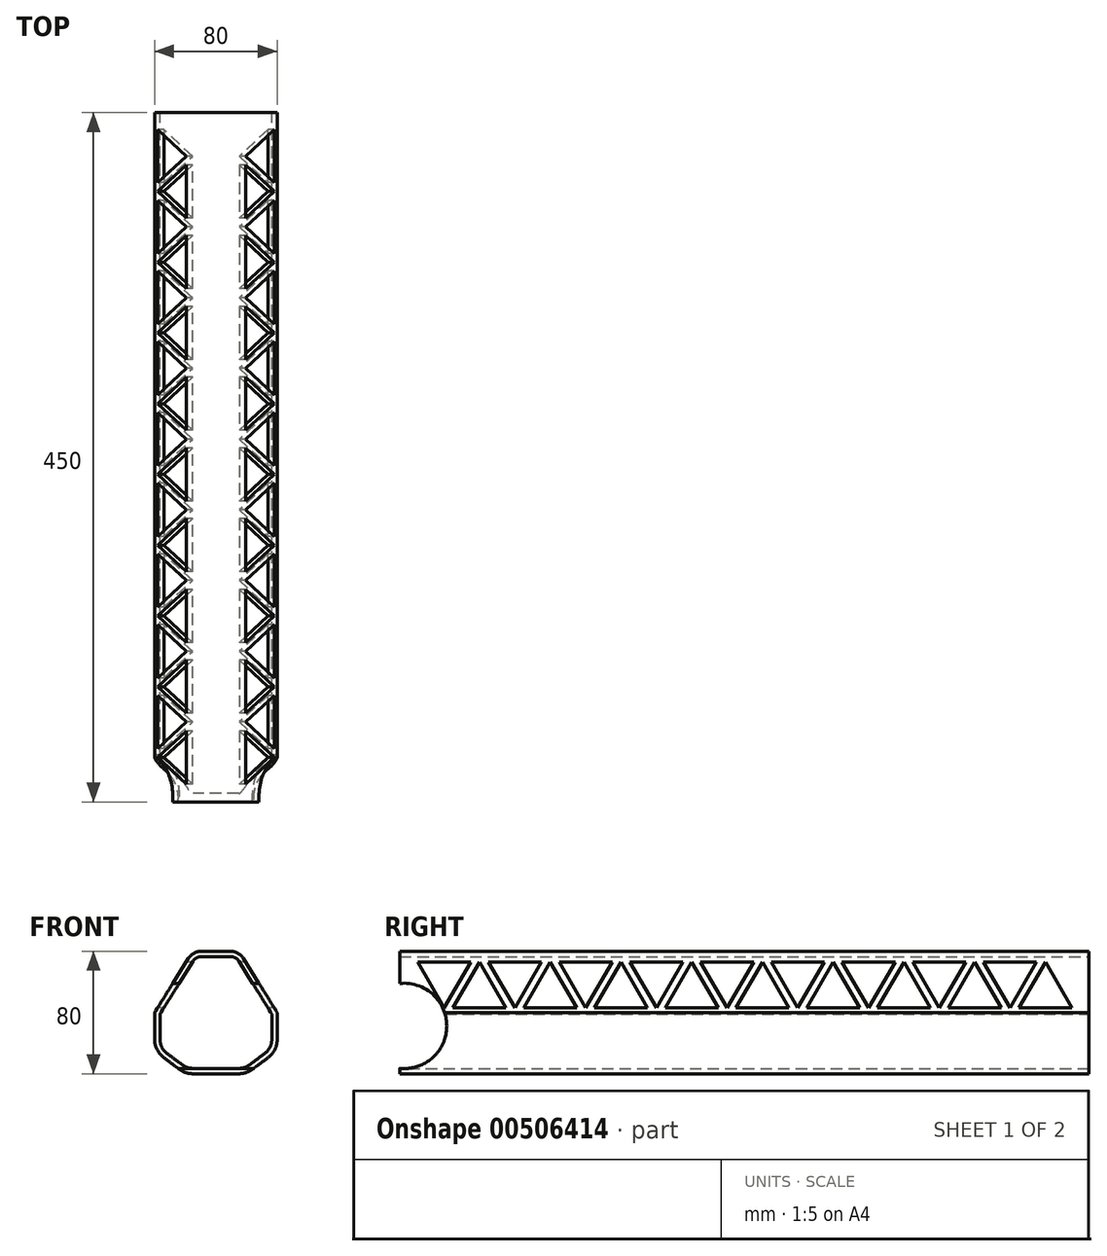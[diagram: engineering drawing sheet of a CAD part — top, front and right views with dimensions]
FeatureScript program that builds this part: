
annotation { "Feature Type Name" : "Feature", "Feature Type Description" : "" }
export const myFeature = defineFeature(function(context is Context, id is Id, definition is map)
    precondition{}
    {
        {
            var Q0;
            Q0=qCreatedBy(makeId("Front.planeOp"),FACE);
            var sketch = newSketch(context, id + "F0", { "sketchPlane" : qUnion([Q0])});
            skLineSegment(sketch, "E0", {"start": v(-40, 5) * mm, "end": v(-40, -20) * mm});
            skLineSegment(sketch, "E1", {"start": v(-40, -20) * mm, "end": v(-20, -35) * mm});
            skLineSegment(sketch, "E2", {"start": v(-20, -35) * mm, "end": v(20, -35) * mm});
            skLineSegment(sketch, "E3", {"start": v(20, -35) * mm, "end": v(40, -20) * mm});
            skLineSegment(sketch, "E4", {"start": v(40, -20) * mm, "end": v(40, 5) * mm});
            skLineSegment(sketch, "E5", {"start": v(40, 5) * mm, "end": v(15, 45) * mm});
            skLineSegment(sketch, "E6", {"start": v(15, 45) * mm, "end": v(-15, 45) * mm});
            skLineSegment(sketch, "E7", {"start": v(-15, 45) * mm, "end": v(-40, 5) * mm});
            skSolve(sketch);
        }
        {
            var Q0;
            Q0=makeQuery(id+"F0.imprint","IMPRINT",FACE,{"disambiguationData":[TD([[makeQuery(id+"F0.imprint","IMPRINT",EDGE,{"derivedFrom":sQuery(id+"F0.wireOp",EDGE,"E0")}),1.0]])]});
            extrude(context, id + "F1", {"entities" : qUnion([Q0]), "depth" : 450 * mm});
        }
        {
            var Q0;
            Q0=makeQuery(id+"F1.opExtrude","SWEPT_EDGE",EDGE,{"disambiguationData":[OSD([sQuery(id+"F0.wireOp",EDGE,"E1"),sQuery(id+"F0.wireOp",EDGE,"E2")])]});
            var Q1;
            Q1=makeQuery(id+"F1.opExtrude","SWEPT_EDGE",EDGE,{"disambiguationData":[OSD([sQuery(id+"F0.wireOp",EDGE,"E0"),sQuery(id+"F0.wireOp",EDGE,"E1")])]});
            var Q2;
            Q2=makeQuery(id+"F1.opExtrude","SWEPT_EDGE",EDGE,{"disambiguationData":[OSD([sQuery(id+"F0.wireOp",EDGE,"E2"),sQuery(id+"F0.wireOp",EDGE,"E3")])]});
            var Q3;
            Q3=makeQuery(id+"F1.opExtrude","SWEPT_EDGE",EDGE,{"disambiguationData":[OSD([sQuery(id+"F0.wireOp",EDGE,"E3"),sQuery(id+"F0.wireOp",EDGE,"E4")])]});
            fillet(context, id + "F2", {"entities" : qUnion([Q0, Q1, Q2, Q3]), "radius" : 15 * mm, "allowEdgeOverflow" : false});
        }
        {
            var Q0;
            Q0=makeQuery(id+"F1.opExtrude","SWEPT_EDGE",EDGE,{"disambiguationData":[OSD([sQuery(id+"F0.wireOp",EDGE,"E5"),sQuery(id+"F0.wireOp",EDGE,"E6")])]});
            var Q1;
            Q1=makeQuery(id+"F1.opExtrude","SWEPT_EDGE",EDGE,{"disambiguationData":[OSD([sQuery(id+"F0.wireOp",EDGE,"E6"),sQuery(id+"F0.wireOp",EDGE,"E7")])]});
            fillet(context, id + "F3", {"entities" : qUnion([Q0, Q1]), "radius" : 10 * mm, "tangentPropagation" : true, "allowEdgeOverflow" : false});
        }
        {
            var Q0;
            Q0=makeQuery(id+"F1.opExtrude","CAP_FACE",FACE,{"disambiguationData":[OSD([sQuery(id+"F0.wireOp",EDGE,"E0"),sQuery(id+"F0.wireOp",EDGE,"E1"),sQuery(id+"F0.wireOp",EDGE,"E2"),sQuery(id+"F0.wireOp",EDGE,"E3"),sQuery(id+"F0.wireOp",EDGE,"E4"),sQuery(id+"F0.wireOp",EDGE,"E5"),sQuery(id+"F0.wireOp",EDGE,"E6"),sQuery(id+"F0.wireOp",EDGE,"E7")])],"isStart":false});
            var Q1;
            Q1=makeQuery(id+"F1.opExtrude","CAP_FACE",FACE,{"disambiguationData":[OSD([sQuery(id+"F0.wireOp",EDGE,"E0"),sQuery(id+"F0.wireOp",EDGE,"E1"),sQuery(id+"F0.wireOp",EDGE,"E2"),sQuery(id+"F0.wireOp",EDGE,"E3"),sQuery(id+"F0.wireOp",EDGE,"E4"),sQuery(id+"F0.wireOp",EDGE,"E5"),sQuery(id+"F0.wireOp",EDGE,"E6"),sQuery(id+"F0.wireOp",EDGE,"E7")])],"isStart":true});
            shell(context, id + "F4", {"entities" : qUnion([Q0, Q1]), "thickness" : 3.5 * mm});
        }
        {
            var Q0;
            Q0=makeQuery(id+"F1.opExtrude","SWEPT_FACE",FACE,{"disambiguationData":[OSD([sQuery(id+"F0.wireOp",EDGE,"E0")])]});
            var sketch = newSketch(context, id + "F5", { "sketchPlane" : qUnion([Q0])});
            skCircle(sketch, "E8.cCircle", {"center": v(28.38, 18) * mm, "radius": 10 * mm, "construction": true});
            skLineSegment(sketch, "E8.0", {"start": v(45.7, 8) * mm, "end": v(11.06, 8) * mm});
            skLineSegment(sketch, "E8.1", {"start": v(11.06, 8) * mm, "end": v(28.38, 38) * mm});
            skLineSegment(sketch, "E8.2", {"start": v(28.38, 38) * mm, "end": v(45.7, 8) * mm});
            skPoint(sketch, "E8.0.midPoint", {"position": v(28.38, 8) * mm});
            skCircle(sketch, "E9.cCircle", {"center": v(51.47, 28) * mm, "radius": 10 * mm, "construction": true});
            skLineSegment(sketch, "E9.0", {"start": v(68.8, 38) * mm, "end": v(51.47, 8) * mm});
            skLineSegment(sketch, "E9.1", {"start": v(51.47, 8) * mm, "end": v(34.15, 38) * mm});
            skLineSegment(sketch, "E9.2", {"start": v(34.15, 38) * mm, "end": v(68.8, 38) * mm});
            skPoint(sketch, "E9.0.midPoint", {"position": v(60.13, 23) * mm});
            skLineSegment(sketch, "E10.1.0.0", {"start": v(80.34, 38) * mm, "end": v(114.98, 38) * mm});
            skPoint(sketch, "E10.1.0.1", {"position": v(74.57, 8) * mm});
            skPoint(sketch, "E10.1.0.2", {"position": v(106.32, 23) * mm});
            skCircle(sketch, "E10.1.0.3", {"center": v(74.57, 18) * mm, "radius": 10 * mm, "construction": true});
            skLineSegment(sketch, "E10.1.0.4", {"start": v(97.66, 8) * mm, "end": v(80.34, 38) * mm});
            skLineSegment(sketch, "E10.1.0.5", {"start": v(114.98, 38) * mm, "end": v(97.66, 8) * mm});
            skCircle(sketch, "E10.1.0.6", {"center": v(97.66, 28) * mm, "radius": 10 * mm, "construction": true});
            skLineSegment(sketch, "E10.1.0.7", {"start": v(74.57, 38) * mm, "end": v(91.89, 8) * mm});
            skLineSegment(sketch, "E10.1.0.8", {"start": v(57.24, 8) * mm, "end": v(74.57, 38) * mm});
            skLineSegment(sketch, "E10.1.0.9", {"start": v(91.89, 8) * mm, "end": v(57.24, 8) * mm});
            skLineSegment(sketch, "E10.2.0.0", {"start": v(126.53, 38) * mm, "end": v(161.17, 38) * mm});
            skPoint(sketch, "E10.2.0.1", {"position": v(120.75, 8) * mm});
            skPoint(sketch, "E10.2.0.2", {"position": v(152.5, 23) * mm});
            skCircle(sketch, "E10.2.0.3", {"center": v(120.75, 18) * mm, "radius": 10 * mm, "construction": true});
            skLineSegment(sketch, "E10.2.0.4", {"start": v(143.85, 8) * mm, "end": v(126.53, 38) * mm});
            skLineSegment(sketch, "E10.2.0.5", {"start": v(161.17, 38) * mm, "end": v(143.85, 8) * mm});
            skCircle(sketch, "E10.2.0.6", {"center": v(143.85, 28) * mm, "radius": 10 * mm, "construction": true});
            skLineSegment(sketch, "E10.2.0.7", {"start": v(120.75, 38) * mm, "end": v(138.07, 8) * mm});
            skLineSegment(sketch, "E10.2.0.8", {"start": v(103.43, 8) * mm, "end": v(120.75, 38) * mm});
            skLineSegment(sketch, "E10.2.0.9", {"start": v(138.07, 8) * mm, "end": v(103.43, 8) * mm});
            skLineSegment(sketch, "E10.3.0.0", {"start": v(172.72, 38) * mm, "end": v(207.36, 38) * mm});
            skPoint(sketch, "E10.3.0.1", {"position": v(166.94, 8) * mm});
            skPoint(sketch, "E10.3.0.2", {"position": v(198.7, 23) * mm});
            skCircle(sketch, "E10.3.0.3", {"center": v(166.94, 18) * mm, "radius": 10 * mm, "construction": true});
            skLineSegment(sketch, "E10.3.0.4", {"start": v(190.04, 8) * mm, "end": v(172.72, 38) * mm});
            skLineSegment(sketch, "E10.3.0.5", {"start": v(207.36, 38) * mm, "end": v(190.04, 8) * mm});
            skCircle(sketch, "E10.3.0.6", {"center": v(190.04, 28) * mm, "radius": 10 * mm, "construction": true});
            skLineSegment(sketch, "E10.3.0.7", {"start": v(166.94, 38) * mm, "end": v(184.26, 8) * mm});
            skLineSegment(sketch, "E10.3.0.8", {"start": v(149.62, 8) * mm, "end": v(166.94, 38) * mm});
            skLineSegment(sketch, "E10.3.0.9", {"start": v(184.26, 8) * mm, "end": v(149.62, 8) * mm});
            skLineSegment(sketch, "E10.4.0.0", {"start": v(218.9, 38) * mm, "end": v(253.55, 38) * mm});
            skPoint(sketch, "E10.4.0.1", {"position": v(213.13, 8) * mm});
            skPoint(sketch, "E10.4.0.2", {"position": v(244.89, 23) * mm});
            skCircle(sketch, "E10.4.0.3", {"center": v(213.13, 18) * mm, "radius": 10 * mm, "construction": true});
            skLineSegment(sketch, "E10.4.0.4", {"start": v(236.23, 8) * mm, "end": v(218.9, 38) * mm});
            skLineSegment(sketch, "E10.4.0.5", {"start": v(253.55, 38) * mm, "end": v(236.23, 8) * mm});
            skCircle(sketch, "E10.4.0.6", {"center": v(236.23, 28) * mm, "radius": 10 * mm, "construction": true});
            skLineSegment(sketch, "E10.4.0.7", {"start": v(213.13, 38) * mm, "end": v(230.45, 8) * mm});
            skLineSegment(sketch, "E10.4.0.8", {"start": v(195.81, 8) * mm, "end": v(213.13, 38) * mm});
            skLineSegment(sketch, "E10.4.0.9", {"start": v(230.45, 8) * mm, "end": v(195.81, 8) * mm});
            skLineSegment(sketch, "E10.5.0.0", {"start": v(265.1, 38) * mm, "end": v(299.74, 38) * mm});
            skPoint(sketch, "E10.5.0.1", {"position": v(259.32, 8) * mm});
            skPoint(sketch, "E10.5.0.2", {"position": v(291.08, 23) * mm});
            skCircle(sketch, "E10.5.0.3", {"center": v(259.32, 18) * mm, "radius": 10 * mm, "construction": true});
            skLineSegment(sketch, "E10.5.0.4", {"start": v(282.42, 8) * mm, "end": v(265.1, 38) * mm});
            skLineSegment(sketch, "E10.5.0.5", {"start": v(299.74, 38) * mm, "end": v(282.42, 8) * mm});
            skCircle(sketch, "E10.5.0.6", {"center": v(282.42, 28) * mm, "radius": 10 * mm, "construction": true});
            skLineSegment(sketch, "E10.5.0.7", {"start": v(259.32, 38) * mm, "end": v(276.64, 8) * mm});
            skLineSegment(sketch, "E10.5.0.8", {"start": v(242, 8) * mm, "end": v(259.32, 38) * mm});
            skLineSegment(sketch, "E10.5.0.9", {"start": v(276.64, 8) * mm, "end": v(242, 8) * mm});
            skLineSegment(sketch, "E10.6.0.0", {"start": v(311.28, 38) * mm, "end": v(345.92, 38) * mm});
            skPoint(sketch, "E10.6.0.1", {"position": v(305.51, 8) * mm});
            skPoint(sketch, "E10.6.0.2", {"position": v(337.26, 23) * mm});
            skCircle(sketch, "E10.6.0.3", {"center": v(305.51, 18) * mm, "radius": 10 * mm, "construction": true});
            skLineSegment(sketch, "E10.6.0.4", {"start": v(328.6, 8) * mm, "end": v(311.28, 38) * mm});
            skLineSegment(sketch, "E10.6.0.5", {"start": v(345.92, 38) * mm, "end": v(328.6, 8) * mm});
            skCircle(sketch, "E10.6.0.6", {"center": v(328.6, 28) * mm, "radius": 10 * mm, "construction": true});
            skLineSegment(sketch, "E10.6.0.7", {"start": v(305.51, 38) * mm, "end": v(322.83, 8) * mm});
            skLineSegment(sketch, "E10.6.0.8", {"start": v(288.19, 8) * mm, "end": v(305.51, 38) * mm});
            skLineSegment(sketch, "E10.6.0.9", {"start": v(322.83, 8) * mm, "end": v(288.19, 8) * mm});
            skLineSegment(sketch, "E10.7.0.0", {"start": v(357.47, 38) * mm, "end": v(392.11, 38) * mm});
            skPoint(sketch, "E10.7.0.1", {"position": v(351.7, 8) * mm});
            skPoint(sketch, "E10.7.0.2", {"position": v(383.45, 23) * mm});
            skCircle(sketch, "E10.7.0.3", {"center": v(351.7, 18) * mm, "radius": 10 * mm, "construction": true});
            skLineSegment(sketch, "E10.7.0.4", {"start": v(374.8, 8) * mm, "end": v(357.47, 38) * mm});
            skLineSegment(sketch, "E10.7.0.5", {"start": v(392.11, 38) * mm, "end": v(374.8, 8) * mm});
            skCircle(sketch, "E10.7.0.6", {"center": v(374.8, 28) * mm, "radius": 10 * mm, "construction": true});
            skLineSegment(sketch, "E10.7.0.7", {"start": v(351.7, 38) * mm, "end": v(369.02, 8) * mm});
            skLineSegment(sketch, "E10.7.0.8", {"start": v(334.38, 8) * mm, "end": v(351.7, 38) * mm});
            skLineSegment(sketch, "E10.7.0.9", {"start": v(369.02, 8) * mm, "end": v(334.38, 8) * mm});
            skLineSegment(sketch, "E10.8.0.0", {"start": v(403.66, 38) * mm, "end": v(438.3, 38) * mm});
            skPoint(sketch, "E10.8.0.1", {"position": v(397.89, 8) * mm});
            skPoint(sketch, "E10.8.0.2", {"position": v(429.64, 23) * mm});
            skCircle(sketch, "E10.8.0.3", {"center": v(397.89, 18) * mm, "radius": 10 * mm, "construction": true});
            skLineSegment(sketch, "E10.8.0.4", {"start": v(420.98, 8) * mm, "end": v(403.66, 38) * mm});
            skLineSegment(sketch, "E10.8.0.5", {"start": v(438.3, 38) * mm, "end": v(420.98, 8) * mm});
            skCircle(sketch, "E10.8.0.6", {"center": v(420.98, 28) * mm, "radius": 10 * mm, "construction": true});
            skLineSegment(sketch, "E10.8.0.7", {"start": v(397.89, 38) * mm, "end": v(415.2, 8) * mm});
            skLineSegment(sketch, "E10.8.0.8", {"start": v(380.57, 8) * mm, "end": v(397.89, 38) * mm});
            skLineSegment(sketch, "E10.8.0.9", {"start": v(415.2, 8) * mm, "end": v(380.57, 8) * mm});
            skLineSegment(sketch, "E10.direction1", {"start": v(11.06, 8) * mm, "end": v(57.24, 8) * mm, "construction": true});
            skSolve(sketch);
        }
        {
            var Q0;
            Q0=makeQuery(id+"F5.imprint","IMPRINT",FACE,{"disambiguationData":[TD([[makeQuery(id+"F5.imprint","IMPRINT",EDGE,{"derivedFrom":sQuery(id+"F5.wireOp",EDGE,"E10.8.0.7")}),-1.0]])]});
            var Q1;
            Q1=makeQuery(id+"F5.imprint","IMPRINT",FACE,{"disambiguationData":[TD([[makeQuery(id+"F5.imprint","IMPRINT",EDGE,{"derivedFrom":sQuery(id+"F5.wireOp",EDGE,"E10.8.0.0")}),-1.0]])]});
            var Q2;
            Q2=makeQuery(id+"F5.imprint","IMPRINT",FACE,{"disambiguationData":[TD([[makeQuery(id+"F5.imprint","IMPRINT",EDGE,{"derivedFrom":sQuery(id+"F5.wireOp",EDGE,"E10.7.0.7")}),-1.0]])]});
            var Q3;
            Q3=makeQuery(id+"F5.imprint","IMPRINT",FACE,{"disambiguationData":[TD([[makeQuery(id+"F5.imprint","IMPRINT",EDGE,{"derivedFrom":sQuery(id+"F5.wireOp",EDGE,"E10.6.0.7")}),-1.0]])]});
            var Q4;
            Q4=makeQuery(id+"F5.imprint","IMPRINT",FACE,{"disambiguationData":[TD([[makeQuery(id+"F5.imprint","IMPRINT",EDGE,{"derivedFrom":sQuery(id+"F5.wireOp",EDGE,"E10.7.0.0")}),-1.0]])]});
            var Q5;
            Q5=makeQuery(id+"F5.imprint","IMPRINT",FACE,{"disambiguationData":[TD([[makeQuery(id+"F5.imprint","IMPRINT",EDGE,{"derivedFrom":sQuery(id+"F5.wireOp",EDGE,"E8.0")}),-1.0]])]});
            var Q6;
            Q6=makeQuery(id+"F5.imprint","IMPRINT",FACE,{"disambiguationData":[TD([[makeQuery(id+"F5.imprint","IMPRINT",EDGE,{"derivedFrom":sQuery(id+"F5.wireOp",EDGE,"E9.0")}),-1.0]])]});
            var Q7;
            Q7=makeQuery(id+"F5.imprint","IMPRINT",FACE,{"disambiguationData":[TD([[makeQuery(id+"F5.imprint","IMPRINT",EDGE,{"derivedFrom":sQuery(id+"F5.wireOp",EDGE,"E10.1.0.0")}),-1.0]])]});
            var Q8;
            Q8=makeQuery(id+"F5.imprint","IMPRINT",FACE,{"disambiguationData":[TD([[makeQuery(id+"F5.imprint","IMPRINT",EDGE,{"derivedFrom":sQuery(id+"F5.wireOp",EDGE,"E10.1.0.7")}),-1.0]])]});
            var Q9;
            Q9=makeQuery(id+"F5.imprint","IMPRINT",FACE,{"disambiguationData":[TD([[makeQuery(id+"F5.imprint","IMPRINT",EDGE,{"derivedFrom":sQuery(id+"F5.wireOp",EDGE,"E10.2.0.0")}),-1.0]])]});
            var Q10;
            Q10=makeQuery(id+"F5.imprint","IMPRINT",FACE,{"disambiguationData":[TD([[makeQuery(id+"F5.imprint","IMPRINT",EDGE,{"derivedFrom":sQuery(id+"F5.wireOp",EDGE,"E10.2.0.7")}),-1.0]])]});
            var Q11;
            Q11=makeQuery(id+"F5.imprint","IMPRINT",FACE,{"disambiguationData":[TD([[makeQuery(id+"F5.imprint","IMPRINT",EDGE,{"derivedFrom":sQuery(id+"F5.wireOp",EDGE,"E10.3.0.0")}),-1.0]])]});
            var Q12;
            Q12=makeQuery(id+"F5.imprint","IMPRINT",FACE,{"disambiguationData":[TD([[makeQuery(id+"F5.imprint","IMPRINT",EDGE,{"derivedFrom":sQuery(id+"F5.wireOp",EDGE,"E10.3.0.7")}),-1.0]])]});
            var Q13;
            Q13=makeQuery(id+"F5.imprint","IMPRINT",FACE,{"disambiguationData":[TD([[makeQuery(id+"F5.imprint","IMPRINT",EDGE,{"derivedFrom":sQuery(id+"F5.wireOp",EDGE,"E10.4.0.0")}),-1.0]])]});
            var Q14;
            Q14=makeQuery(id+"F5.imprint","IMPRINT",FACE,{"disambiguationData":[TD([[makeQuery(id+"F5.imprint","IMPRINT",EDGE,{"derivedFrom":sQuery(id+"F5.wireOp",EDGE,"E10.4.0.7")}),-1.0]])]});
            var Q15;
            Q15=makeQuery(id+"F5.imprint","IMPRINT",FACE,{"disambiguationData":[TD([[makeQuery(id+"F5.imprint","IMPRINT",EDGE,{"derivedFrom":sQuery(id+"F5.wireOp",EDGE,"E10.5.0.0")}),-1.0]])]});
            var Q16;
            Q16=makeQuery(id+"F5.imprint","IMPRINT",FACE,{"disambiguationData":[TD([[makeQuery(id+"F5.imprint","IMPRINT",EDGE,{"derivedFrom":sQuery(id+"F5.wireOp",EDGE,"E10.5.0.7")}),-1.0]])]});
            var Q17;
            Q17=makeQuery(id+"F5.imprint","IMPRINT",FACE,{"disambiguationData":[TD([[makeQuery(id+"F5.imprint","IMPRINT",EDGE,{"derivedFrom":sQuery(id+"F5.wireOp",EDGE,"E10.6.0.0")}),-1.0]])]});
            extrude(context, id + "F6", {"entities" : qUnion([Q0, Q1, Q2, Q3, Q4, Q5, Q6, Q7, Q8, Q9, Q10, Q11, Q12, Q13, Q14, Q15, Q16, Q17]), "operationType" : NewBodyOperationType.REMOVE, "oppositeDirection" : true, "depth" : 85 * mm});
        }
        {
            var Q0;
            Q0=makeQuery(id+"F1.opExtrude","SWEPT_FACE",FACE,{"disambiguationData":[OSD([sQuery(id+"F0.wireOp",EDGE,"E0")])]});
            var sketch = newSketch(context, id + "F7", { "sketchPlane" : qUnion([Q0])});
            skCircle(sketch, "E11", {"center": v(447.13, -3.75) * mm, "radius": 27.88 * mm});
            skPoint(sketch, "E11.centerSnap0", {"position": v(450, -3.75) * mm});
            skSolve(sketch);
        }
        {
            var Q0;
            Q0 = qSketchRegion(id + "F7", true);
            extrude(context, id + "F8", {"entities" : qUnion([Q0]), "operationType" : NewBodyOperationType.REMOVE, "oppositeDirection" : true, "depth" : 85 * mm});
        }
    });
